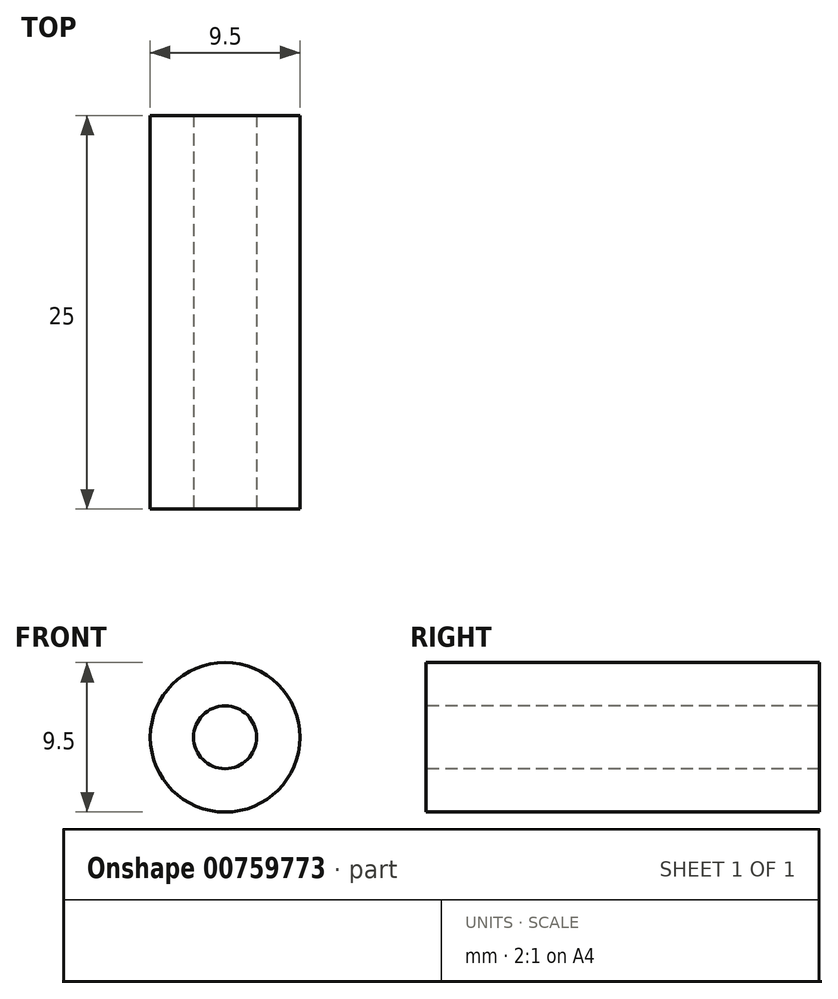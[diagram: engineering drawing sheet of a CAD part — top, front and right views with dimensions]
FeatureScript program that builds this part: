
annotation { "Feature Type Name" : "Feature", "Feature Type Description" : "" }
export const myFeature = defineFeature(function(context is Context, id is Id, definition is map)
    precondition{}
    {
        {
            var Q0;
            Q0=qCreatedBy(makeId("Front.planeOp"),FACE);
            var sketch = newSketch(context, id + "F0", { "sketchPlane" : qUnion([Q0])});
            skCircle(sketch, "E0", {"center": v(0, 0) * mm, "radius": 4.75 * mm});
            skSolve(sketch);
        }
        {
            var Q0;
            Q0=makeQuery(id+"F0.imprint","IMPRINT",FACE,{"disambiguationData":[TD([[makeQuery(id+"F0.imprint","IMPRINT",EDGE,{"derivedFrom":sQuery(id+"F0.wireOp",EDGE,"E0")}),1.0]])]});
            var sketch = newSketch(context, id + "F1", { "sketchPlane" : qUnion([Q0])});
            skCircle(sketch, "E1", {"center": v(0, 0) * mm, "radius": 2 * mm});
            skSolve(sketch);
        }
        {
            var Q0;
            Q0=sQuery(id+"F0.wireOp",EDGE,"E0");
            extrude(context, id + "F2", {"bodyType" : ToolBodyType.SURFACE, "surfaceEntities" : qUnion([Q0]), "depth" : 25 * mm, "offsetDistance" : 25 * mm});
        }
        {
            var Q0;
            Q0=sQuery(id+"F1.wireOp",EDGE,"E1");
            extrude(context, id + "F3", {"bodyType" : ToolBodyType.SURFACE, "surfaceEntities" : qUnion([Q0]), "depth" : 25 * mm, "offsetDistance" : 25 * mm});
        }
    });
